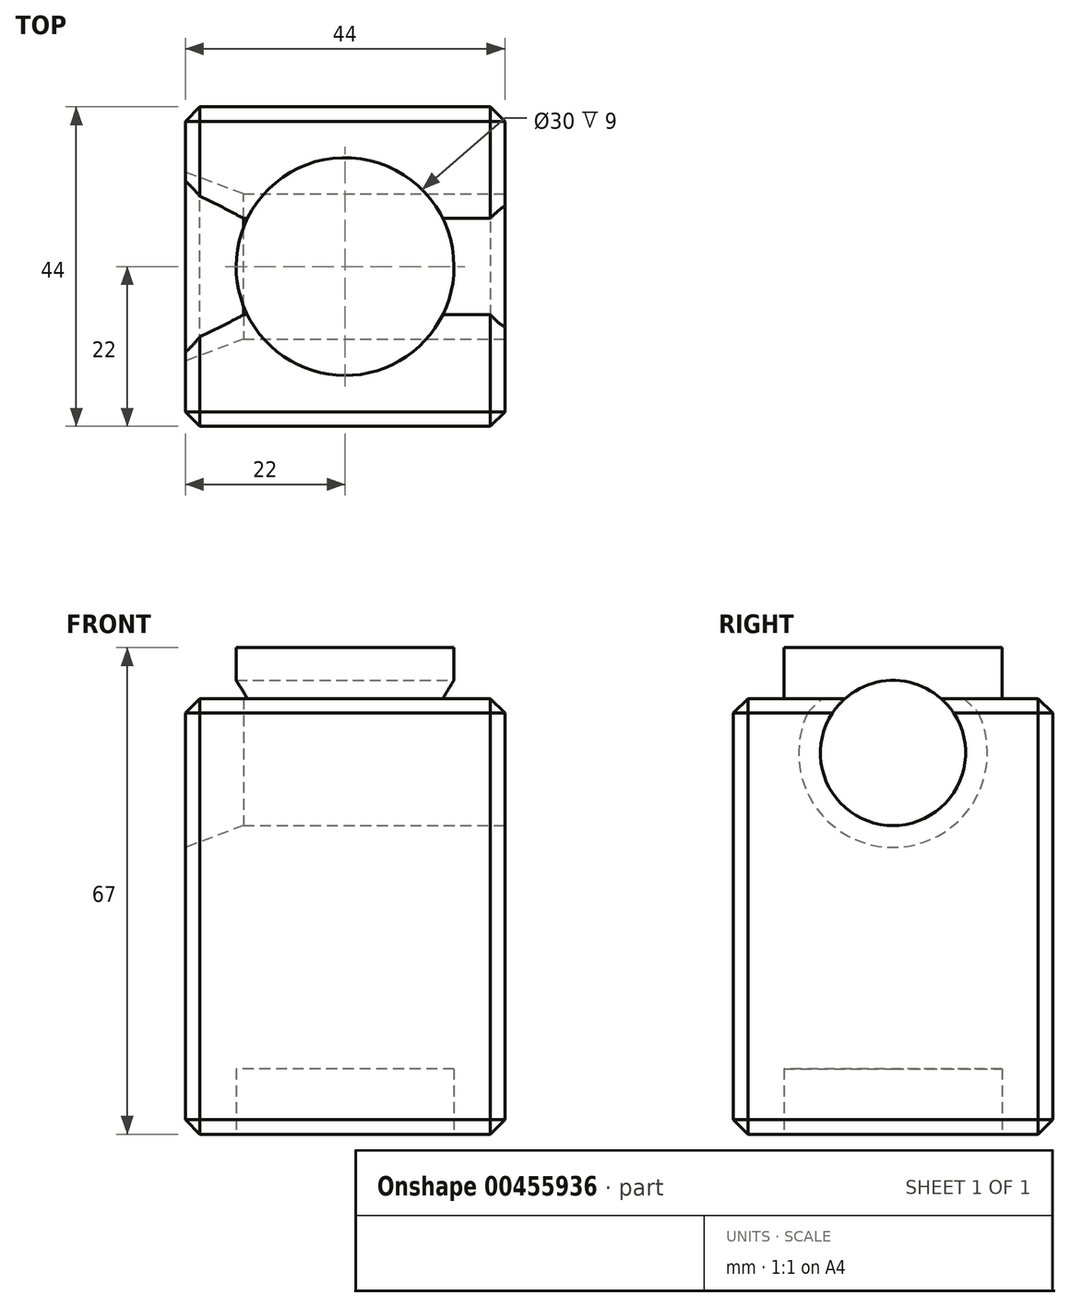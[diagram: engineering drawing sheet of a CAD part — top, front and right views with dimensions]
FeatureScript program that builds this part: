
annotation { "Feature Type Name" : "Feature", "Feature Type Description" : "" }
export const myFeature = defineFeature(function(context is Context, id is Id, definition is map)
    precondition{}
    {
        {
            assignVariable(context, id + "F0", {"name" : "H", "anyValue" : 60});
        }
        {
            assignVariable(context, id + "F1", {"name" : "h", "anyValue" : 7});
        }
        {
            var Q0;
            Q0=qCreatedBy(makeId("Top.planeOp"),FACE);
            var sketch = newSketch(context, id + "F2", { "sketchPlane" : qUnion([Q0])});
            skLineSegment(sketch, "E0.bottom", {"start": v(-22, 22) * mm, "end": v(22, 22) * mm});
            skLineSegment(sketch, "E0.top", {"start": v(-22, -22) * mm, "end": v(22, -22) * mm});
            skLineSegment(sketch, "E0.left", {"start": v(-22, 22) * mm, "end": v(-22, -22) * mm});
            skLineSegment(sketch, "E0.right", {"start": v(22, 22) * mm, "end": v(22, -22) * mm});
            skPoint(sketch, "E1", {"position": v(-22, 0) * mm});
            skPoint(sketch, "E2", {"position": v(0, 22) * mm});
            skCircle(sketch, "E3", {"center": v(0, 0) * mm, "radius": 15 * mm});
            skCircle(sketch, "E4", {"center": v(0, 0) * mm, "radius": 10 * mm});
            skSolve(sketch);
        }
        {
            var Q0;
            Q0=makeQuery(id+"F2.imprint","IMPRINT",FACE,{"disambiguationData":[TD([[makeQuery(id+"F2.imprint","IMPRINT",EDGE,{"derivedFrom":sQuery(id+"F2.wireOp",EDGE,"E0.bottom")}),-1.0]])]});
            var Q1;
            Q1=makeQuery(id+"F2.imprint","IMPRINT",FACE,{"disambiguationData":[TD([[makeQuery(id+"F2.imprint","IMPRINT",EDGE,{"derivedFrom":sQuery(id+"F2.wireOp",EDGE,"E3")}),1.0]])]});
            var Q2;
            Q2=makeQuery(id+"F2.imprint","IMPRINT",FACE,{"disambiguationData":[TD([[makeQuery(id+"F2.imprint","IMPRINT",EDGE,{"derivedFrom":sQuery(id+"F2.wireOp",EDGE,"E4")}),1.0]])]});
            extrude(context, id + "F3", {"entities" : qUnion([Q0, Q1, Q2]), "depth" : (getVariable(context, 'H')) * mm});
        }
        {
            var Q0;
            Q0=makeQuery(id+"F3.opExtrude","CAP_FACE",FACE,{"disambiguationData":[OSD([sQuery(id+"F2.wireOp",EDGE,"E0.bottom"),sQuery(id+"F2.wireOp",EDGE,"E0.top"),sQuery(id+"F2.wireOp",EDGE,"E0.left"),sQuery(id+"F2.wireOp",EDGE,"E0.right")])],"isStart":false});
            var sketch = newSketch(context, id + "F4", { "sketchPlane" : qUnion([Q0])});
            skLineSegment(sketch, "E5.bottom", {"start": v(-22, 22) * mm, "end": v(22, 22) * mm});
            skLineSegment(sketch, "E5.top", {"start": v(-22, -22) * mm, "end": v(22, -22) * mm});
            skLineSegment(sketch, "E5.left", {"start": v(-22, 22) * mm, "end": v(-22, -22) * mm});
            skLineSegment(sketch, "E5.right", {"start": v(22, 22) * mm, "end": v(22, -22) * mm});
            skPoint(sketch, "E6", {"position": v(-22, 0) * mm});
            skPoint(sketch, "E7", {"position": v(0, 22) * mm});
            skCircle(sketch, "E8", {"center": v(0, 0) * mm, "radius": 15 * mm});
            skCircle(sketch, "E9", {"center": v(0, 0) * mm, "radius": 10 * mm});
            skSolve(sketch);
        }
        {
            var Q0;
            Q0=makeQuery(id+"F4.imprint","IMPRINT",FACE,{"disambiguationData":[TD([[makeQuery(id+"F4.imprint","IMPRINT",EDGE,{"derivedFrom":sQuery(id+"F4.wireOp",EDGE,"E8")}),1.0]])]});
            var Q1;
            Q1=makeQuery(id+"F4.imprint","IMPRINT",FACE,{"disambiguationData":[TD([[makeQuery(id+"F4.imprint","IMPRINT",EDGE,{"derivedFrom":sQuery(id+"F4.wireOp",EDGE,"E9")}),1.0]])]});
            extrude(context, id + "F5", {"entities" : qUnion([Q0, Q1]), "operationType" : NewBodyOperationType.ADD, "depth" : (getVariable(context, 'h')) * mm});
        }
        {
            var Q0;
            Q0=makeQuery(id+"F2.imprint","IMPRINT",FACE,{"disambiguationData":[TD([[makeQuery(id+"F2.imprint","IMPRINT",EDGE,{"derivedFrom":sQuery(id+"F2.wireOp",EDGE,"E3")}),1.0]])]});
            var Q1;
            Q1=makeQuery(id+"F2.imprint","IMPRINT",FACE,{"disambiguationData":[TD([[makeQuery(id+"F2.imprint","IMPRINT",EDGE,{"derivedFrom":sQuery(id+"F2.wireOp",EDGE,"E4")}),1.0]])]});
            extrude(context, id + "F6", {"entities" : qUnion([Q0, Q1]), "operationType" : NewBodyOperationType.REMOVE, "depth" : (getVariable(context, 'h') + 2) * mm});
        }
        {
            assignVariable(context, id + "F7", {"name" : "c", "anyValue" : 2});
        }
        {
            var Q0;
            Q0=makeQuery(id+"F3.opExtrude","CAP_EDGE",EDGE,{"disambiguationData":[OSD([sQuery(id+"F2.wireOp",EDGE,"E0.top")])],"isStart":true});
            var Q1;
            Q1=makeQuery(id+"F3.opExtrude","CAP_EDGE",EDGE,{"disambiguationData":[OSD([sQuery(id+"F2.wireOp",EDGE,"E0.right")])],"isStart":true});
            var Q2;
            Q2=makeQuery(id+"F3.opExtrude","CAP_EDGE",EDGE,{"disambiguationData":[OSD([sQuery(id+"F2.wireOp",EDGE,"E0.left")])],"isStart":true});
            var Q3;
            Q3=makeQuery(id+"F3.opExtrude","CAP_EDGE",EDGE,{"disambiguationData":[OSD([sQuery(id+"F2.wireOp",EDGE,"E0.bottom")])],"isStart":true});
            var Q4;
            Q4=makeQuery(id+"F3.opExtrude","SWEPT_EDGE",EDGE,{"disambiguationData":[OSD([sQuery(id+"F2.wireOp",EDGE,"E0.top"),sQuery(id+"F2.wireOp",EDGE,"E0.left")])]});
            var Q5;
            Q5=makeQuery(id+"F3.opExtrude","SWEPT_EDGE",EDGE,{"disambiguationData":[OSD([sQuery(id+"F2.wireOp",EDGE,"E0.bottom"),sQuery(id+"F2.wireOp",EDGE,"E0.left")])]});
            var Q6;
            Q6=makeQuery(id+"F3.opExtrude","SWEPT_EDGE",EDGE,{"disambiguationData":[OSD([sQuery(id+"F2.wireOp",EDGE,"E0.bottom"),sQuery(id+"F2.wireOp",EDGE,"E0.right")])]});
            var Q7;
            Q7=makeQuery(id+"F3.opExtrude","SWEPT_EDGE",EDGE,{"disambiguationData":[OSD([sQuery(id+"F2.wireOp",EDGE,"E0.top"),sQuery(id+"F2.wireOp",EDGE,"E0.right")])]});
            var Q8;
            Q8=makeQuery(id+"F3.opExtrude","CAP_EDGE",EDGE,{"disambiguationData":[OSD([sQuery(id+"F2.wireOp",EDGE,"E0.right")])],"isStart":false});
            var Q9;
            Q9=makeQuery(id+"F3.opExtrude","CAP_EDGE",EDGE,{"disambiguationData":[OSD([sQuery(id+"F2.wireOp",EDGE,"E0.top")])],"isStart":false});
            var Q10;
            Q10=makeQuery(id+"F3.opExtrude","CAP_EDGE",EDGE,{"disambiguationData":[OSD([sQuery(id+"F2.wireOp",EDGE,"E0.left")])],"isStart":false});
            var Q11;
            Q11=makeQuery(id+"F3.opExtrude","CAP_EDGE",EDGE,{"disambiguationData":[OSD([sQuery(id+"F2.wireOp",EDGE,"E0.bottom")])],"isStart":false});
            var Q12;
            Q12=makeQuery(id+"F6.boolean.opBoolean","COPY",EDGE,{"derivedFrom":makeQuery(id+"F6.opExtrude","CAP_EDGE",EDGE,{"disambiguationData":[OSD([sQuery(id+"F2.wireOp",EDGE,"E3")])],"isStart":true})});
            chamfer(context, id + "F8", {"entities" : qUnion([Q0, Q1, Q2, Q3, Q4, Q5, Q6, Q7, Q8, Q9, Q10, Q11, Q12]), "width" : (getVariable(context, 'c')) * mm, "tangentPropagation" : true});
        }
        {
            var Q0;
            Q0=makeQuery(id+"F3.opExtrude","SWEPT_FACE",FACE,{"disambiguationData":[OSD([sQuery(id+"F2.wireOp",EDGE,"E0.right")])]});
            cPlane(context, id + "F9", {"entities" : qUnion([Q0]), "cplaneType" : CPlaneType.OFFSET, "offset" : 0 * mm, "width" : 150 * mm, "height" : 150 * mm});
        }
        {
            var Q0;
            Q0=qCreatedBy(id+"F9.planeOp",FACE);
            var sketch = newSketch(context, id + "F10", { "sketchPlane" : qUnion([Q0])});
            skLineSegment(sketch, "E10", {"start": v(0, 67) * mm, "end": v(0, 33.65) * mm});
            skCircle(sketch, "E11", {"center": v(0, 52.5) * mm, "radius": 10 * mm});
            skSolve(sketch);
        }
        {
            var Q0;
            {var subQ0=sQuery(id+"F10.wireOp",EDGE,"E11");var subQ1=sQuery(id+"F10.wireOp",EDGE,"E10");var subQ2=makeQuery(id+"F10.imprint","INTERSECT",VERTEX,{"disambiguationData":[OD(0.0)],"derivedFrom":[subQ1,subQ0]});Q0=makeQuery(id+"F10.imprint","IMPRINT",FACE,{"disambiguationData":[TD([[makeQuery(id+"F10.imprint","IMPRINT",EDGE,{"disambiguationData":[TD([[subQ2,1.0]])],"derivedFrom":subQ1}),-1.0]])]});}
            var Q1;
            {var subQ0=sQuery(id+"F10.wireOp",EDGE,"E11");var subQ1=sQuery(id+"F10.wireOp",EDGE,"E10");var subQ2=makeQuery(id+"F10.imprint","INTERSECT",VERTEX,{"disambiguationData":[OD(0.0)],"derivedFrom":[subQ1,subQ0]});Q1=makeQuery(id+"F10.imprint","IMPRINT",FACE,{"disambiguationData":[TD([[makeQuery(id+"F10.imprint","IMPRINT",EDGE,{"disambiguationData":[TD([[subQ2,1.0]])],"derivedFrom":subQ1}),1.0]])]});}
            extrude(context, id + "F11", {"entities" : qUnion([Q0, Q1]), "operationType" : NewBodyOperationType.REMOVE, "oppositeDirection" : true, "depth" : 60 * mm});
        }
        {
            var Q0;
            Q0=makeQuery(id+"F11.boolean.opBoolean","INTERSECT",EDGE,{"derivedFrom":[makeQuery(id+"F3.opExtrude","SWEPT_FACE",FACE,{"disambiguationData":[OSD([sQuery(id+"F2.wireOp",EDGE,"E0.left")])]}),makeQuery(id+"F11.opExtrude","SWEPT_FACE",FACE,{"disambiguationData":[OSD([sQuery(id+"F10.wireOp",EDGE,"E11")])]})]});
            var Q1;
            Q1=makeQuery(id+"F11.boolean.opBoolean","COPY",EDGE,{"derivedFrom":makeQuery(id+"F11.opExtrude","CAP_EDGE",EDGE,{"disambiguationData":[OSD([sQuery(id+"F10.wireOp",EDGE,"E11")])],"isStart":true})});
            chamfer(context, id + "F12", {"entities" : qUnion([Q0, Q1]), "chamferType" : ChamferType.TWO_OFFSETS, "width1" : 3 * mm, "oppositeDirection" : false, "width2" : 8 * mm, "tangentPropagation" : true});
        }
    });
